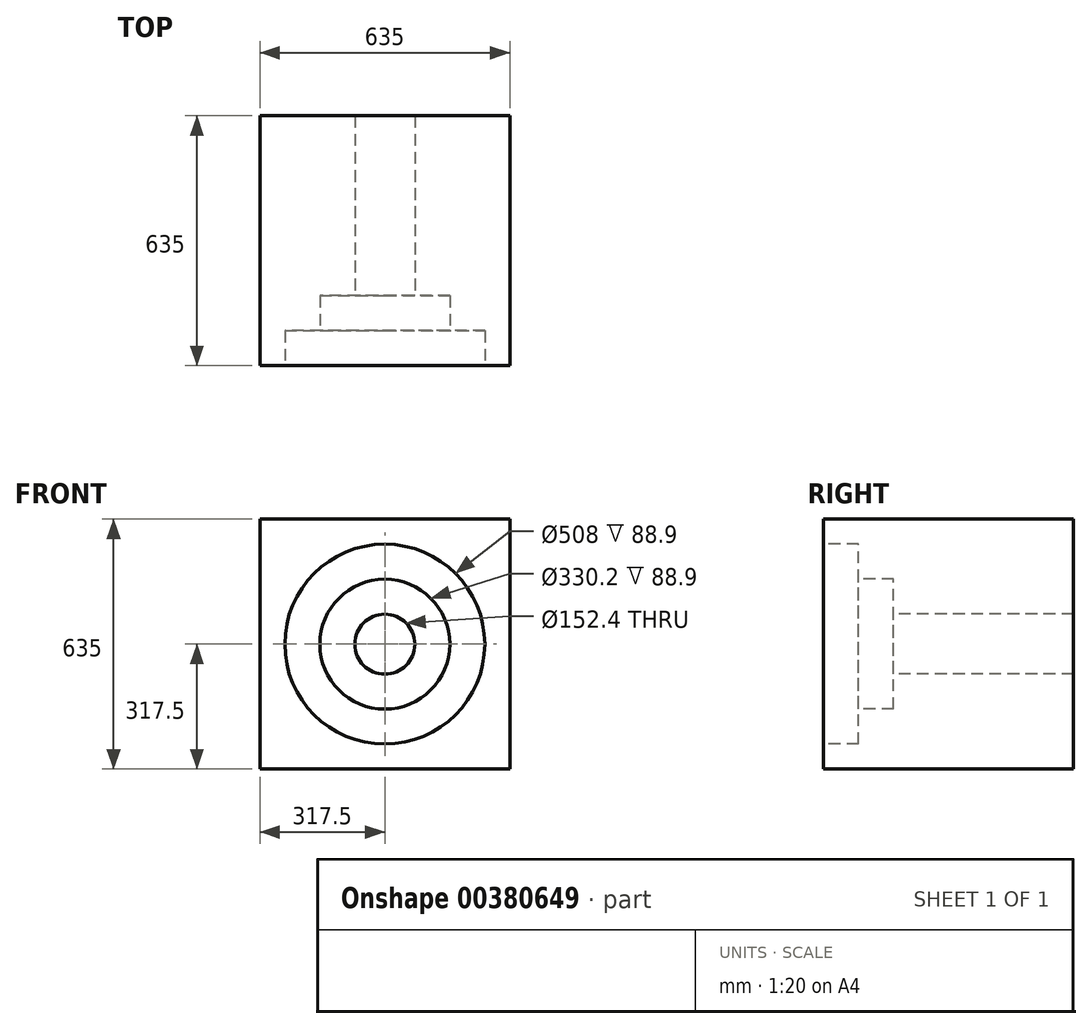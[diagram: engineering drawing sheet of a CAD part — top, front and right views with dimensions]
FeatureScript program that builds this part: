
annotation { "Feature Type Name" : "Feature", "Feature Type Description" : "" }
export const myFeature = defineFeature(function(context is Context, id is Id, definition is map)
    precondition{}
    {
        {
            var Q0;
            Q0=qCreatedBy(makeId("Front.planeOp"),FACE);
            var sketch = newSketch(context, id + "F0", { "sketchPlane" : qUnion([Q0])});
            skLineSegment(sketch, "E0.bottom", {"start": v(317.5, 317.5) * mm, "end": v(-317.5, 317.5) * mm});
            skLineSegment(sketch, "E0.top", {"start": v(317.5, -317.5) * mm, "end": v(-317.5, -317.5) * mm});
            skLineSegment(sketch, "E0.left", {"start": v(317.5, 317.5) * mm, "end": v(317.5, -317.5) * mm});
            skLineSegment(sketch, "E0.right", {"start": v(-317.5, 317.5) * mm, "end": v(-317.5, -317.5) * mm});
            skPoint(sketch, "E0.middle", {"position": v(0, 0) * mm});
            skLineSegment(sketch, "E1", {"start": v(0, 454.82) * mm, "end": v(0, -500.27) * mm});
            skLineSegment(sketch, "E2", {"start": v(-379.76, 0) * mm, "end": v(492.93, 0) * mm});
            skSolve(sketch);
        }
        {
            var Q0;
            Q0 = qSketchRegion(id + "F0", true);
            extrude(context, id + "F1", {"entities" : qUnion([Q0]), "depth" : 317.5 * mm, "hasSecondDirection" : true, "secondDirectionOppositeDirection" : true, "secondDirectionDepth" : 317.5 * mm});
        }
        {
            var Q0;
            Q0=makeQuery(id+"F1.opExtrude","CAP_FACE",FACE,{"disambiguationData":[OSD([sQuery(id+"F0.wireOp",EDGE,"E0.bottom"),sQuery(id+"F0.wireOp",EDGE,"E0.top"),sQuery(id+"F0.wireOp",EDGE,"E0.left"),sQuery(id+"F0.wireOp",EDGE,"E0.right")])],"isStart":false});
            var sketch = newSketch(context, id + "F2", { "sketchPlane" : qUnion([Q0])});
            skCircle(sketch, "E3", {"center": v(0, 0) * mm, "radius": 254 * mm});
            skSolve(sketch);
        }
        {
            var Q0;
            Q0=makeQuery(id+"F2.imprint","IMPRINT",FACE,{"disambiguationData":[TD([[makeQuery(id+"F2.imprint","IMPRINT",EDGE,{"derivedFrom":sQuery(id+"F2.wireOp",EDGE,"E3")}),1.0]])]});
            var Q1;
            Q1=sQuery(id+"F2.wireOp",EDGE,"E3");
            extrude(context, id + "F3", {"entities" : qUnion([Q0]), "operationType" : NewBodyOperationType.REMOVE, "surfaceEntities" : qUnion([Q1]), "oppositeDirection" : true, "depth" : 88.9 * mm});
        }
        {
            var Q0;
            Q0=makeQuery(id+"F3.boolean.opBoolean","COPY",FACE,{"derivedFrom":makeQuery(id+"F3.opExtrude","CAP_FACE",FACE,{"disambiguationData":[OSD([sQuery(id+"F2.wireOp",EDGE,"E3")])],"isStart":false})});
            var sketch = newSketch(context, id + "F4", { "sketchPlane" : qUnion([Q0])});
            skCircle(sketch, "E4", {"center": v(0, 0) * mm, "radius": 165.1 * mm});
            skSolve(sketch);
        }
        {
            var Q0;
            Q0=makeQuery(id+"F4.imprint","IMPRINT",FACE,{"disambiguationData":[TD([[makeQuery(id+"F4.imprint","IMPRINT",EDGE,{"derivedFrom":sQuery(id+"F4.wireOp",EDGE,"E4")}),1.0]])]});
            var Q1;
            Q1=sQuery(id+"F4.wireOp",EDGE,"E4");
            extrude(context, id + "F5", {"entities" : qUnion([Q0]), "operationType" : NewBodyOperationType.REMOVE, "surfaceEntities" : qUnion([Q1]), "oppositeDirection" : true, "depth" : 88.9 * mm});
        }
        {
            var Q0;
            Q0=makeQuery(id+"F5.boolean.opBoolean","COPY",FACE,{"derivedFrom":makeQuery(id+"F5.opExtrude","CAP_FACE",FACE,{"disambiguationData":[OSD([sQuery(id+"F4.wireOp",EDGE,"E4")])],"isStart":false})});
            var sketch = newSketch(context, id + "F6", { "sketchPlane" : qUnion([Q0])});
            skCircle(sketch, "E5", {"center": v(0, 0) * mm, "radius": 76.2 * mm});
            skSolve(sketch);
        }
        {
            var Q0;
            Q0=makeQuery(id+"F6.imprint","IMPRINT",FACE,{"disambiguationData":[TD([[makeQuery(id+"F6.imprint","IMPRINT",EDGE,{"derivedFrom":sQuery(id+"F6.wireOp",EDGE,"E5")}),1.0]])]});
            extrude(context, id + "F7", {"entities" : qUnion([Q0]), "operationType" : NewBodyOperationType.REMOVE, "endBound" : BoundingType.THROUGH_ALL, "oppositeDirection" : true, "depth" : 25.4 * mm});
        }
    });
